# Revit family: NEWSE_Trez_Door_Fast_Rolling
name_source: partatom
category: Specialty Equipment
units: mm (PartAtom-declared; Revit-internal decimal feet)

## family parameters
Cut with Voids When Loaded = No
Host = Face
Maintain Annotation Orientation = No
Part Type = Normal
Room Calculation Point = No
Round Connector Dimension = Use Diameter
Shared = No

## types (5) — shared parameters
Clear Height = 2500 mm  [stored 8.2021 ft]
Description = The door model FR (Fast Rolling) is a fast industrial rolling door with 2 lines of transparent labels for observations. It complies with 2006/42/EC.
Frame Material = TREZ_Steel_Frame
Manufacturer = TREZ Ltd.
Model = FR
Panel Material = TREZ_Steel_Panel
Real Height = 2500 mm  [stored 8.2021 ft]
Trim Material = TREZ_Steel_Frame
URL = https://trez.bg
zero-valued in all types: Default Elevation

## per-type parameters (varying)
| type | Clear Width | Real Width |
| 2900x2500mm | 2900 mm  [stored 9.51444 ft] | 2900 mm  [stored 9.51444 ft] |
| 2300x2500mm | 2300 mm | 2300 mm |
| 2000x2500mm | 2000 mm  [stored 6.56168 ft] | 2000 mm  [stored 6.56168 ft] |
| 3300x2500mm | 3300 mm  [stored 10.8268 ft] | 3300 mm  [stored 10.8268 ft] |
| 3600x2500mm | 3600 mm  [stored 11.811 ft] | 3600 mm  [stored 11.811 ft] |

note: [stored X ft] marks values corroborated as IEEE doubles in the binary element streams (Revit-internal decimal feet)

## geometry (parser evidence)
native form markers: Sweep x2
no freeform markers — native parametric forms only
